# Revit family: РИДАН_Соленоидный клапан EV220WR(DN65_100)
name_source: partatom
category: Арматура трубопроводов
units: mm (PartAtom-declared; Revit-internal decimal feet)

## family parameters
Всегда вертикально = Да
На основе рабочей плоскости = Нет
Общий = Нет
При загрузке вырезать с полостями = Нет
Размер круглого соединителя = Использовать диаметр
Тип детали = Нормальный

## types (9) — shared parameters
ADSK_Версия Revit = 2019
ADSK_Версия семейства = 1.0
ADSK_Единица измерения = шт.
ADSK_Завод-изготовитель = ООО «Ридан-Трейд»
ADSK_Количество = 1
ADSK_Количество фаз = 1
ADSK_Коэффициент мощности = 1
ADSK_Потеря давления жидкости = 0.0 Па
ADSK_Расход жидкости = 0.0 л/с
LT = EV220WR _DN65_100
Table = EV220WR _DN65_100_1

## per-type parameters (varying)
- DN65+RW3220AC: ADSK_Диаметр условный=65 мм; ADSK_Код изделия=016D6065R; ADSK_Марка=EV220WR DN65; ADSK_Масса=15.1; ADSK_Наименование=Клапан электромагнитный EV220WR, G 2 1/2, Ду 65 мм, EPDM, нормально закрытый; ADSK_Напряжение=230 В; ADSK_Номинальная мощность=16 Вт; ADSK_Полная мощность=16 В·А; ADSK_Пропускная способность=12.2 л/с; a=2 мм; b=18 мм; c=10 мм; d=100 мм; e=199 мм; f=78 мм; g=98 мм; h=114 мм; i=118 мм; j=185 мм; k=40 мм; l=74 мм; m=92 мм; n=116 мм; o=178 мм; p=142 мм; r=114 мм; s=42 мм; t=137 мм; t1=158 мм; t2=79 мм; t3=83 мм; Катушка=Влж_Катушка EV220WR : RW3220AC; Катушка_1=RW3220AC; УГО_Длина=259 мм
- DN65+RW3024AC: ADSK_Диаметр условный=65 мм; ADSK_Код изделия=016D6065R; ADSK_Марка=EV220WR DN65; ADSK_Масса=15.1; ADSK_Наименование=Клапан электромагнитный EV220WR, G 2 1/2, Ду 65 мм, EPDM, нормально закрытый; ADSK_Напряжение=24 В; ADSK_Номинальная мощность=24 Вт; ADSK_Полная мощность=24 В·А; ADSK_Пропускная способность=12.2 л/с; a=2 мм; b=18 мм; c=10 мм; d=100 мм; e=199 мм; f=78 мм; g=98 мм; h=114 мм; i=118 мм; j=185 мм; k=40 мм; l=74 мм; m=92 мм; n=116 мм; o=178 мм; p=142 мм; r=114 мм; s=42 мм; t=137 мм; t1=158 мм; t2=79 мм; t3=83 мм; Катушка=Влж_Катушка EV220WR : RW3024AC; Катушка_1=RW3024AC; УГО_Длина=259 мм
- DN65+RW3024DC: ADSK_Диаметр условный=65 мм; ADSK_Код изделия=016D6065R; ADSK_Марка=EV220WR DN65; ADSK_Масса=15.1; ADSK_Наименование=Клапан электромагнитный EV220WR, G 2 1/2, Ду 65 мм, EPDM, нормально закрытый; ADSK_Напряжение=24 В; ADSK_Номинальная мощность=14 Вт; ADSK_Полная мощность=14 В·А; ADSK_Пропускная способность=12.2 л/с; a=2 мм; b=18 мм; c=10 мм; d=100 мм; e=199 мм; f=78 мм; g=98 мм; h=114 мм; i=118 мм; j=185 мм; k=40 мм; l=74 мм; m=92 мм; n=116 мм; o=178 мм; p=142 мм; r=114 мм; s=42 мм; t=137 мм; t1=158 мм; t2=79 мм; t3=83 мм; Катушка=Влж_Катушка EV220WR : RW3024DC; Катушка_1=RW3024DC; УГО_Длина=259 мм
- DN80+RW3220AC: ADSK_Диаметр условный=80 мм; ADSK_Код изделия=016D6080R; ADSK_Марка=EV220WR DN80; ADSK_Масса=17; ADSK_Наименование=Клапан электромагнитный EV220WR, G 3, Ду 80 мм, EPDM, нормально закрытый; ADSK_Напряжение=230 В; ADSK_Номинальная мощность=16 Вт; ADSK_Полная мощность=16 В·А; ADSK_Пропускная способность=19.4 л/с; a=3 мм; b=16 мм; c=38 мм; d=82 мм; e=163 мм; f=93 мм; g=125 мм; h=126 мм; i=132 мм; j=200 мм; k=50 мм; l=86 мм; m=102 мм; n=126 мм; o=195 мм; p=137 мм; r=103 мм; s=42 мм; t=151 мм; t1=174 мм; t2=87 мм; t3=94 мм; Катушка=Влж_Катушка EV220WR : RW3220AC; Катушка_1=RW3220AC; УГО_Длина=278 мм
- DN80+RW3024AC: ADSK_Диаметр условный=80 мм; ADSK_Код изделия=016D6080R; ADSK_Марка=EV220WR DN80; ADSK_Масса=17; ADSK_Наименование=Клапан электромагнитный EV220WR, G 3, Ду 80 мм, EPDM, нормально закрытый; ADSK_Напряжение=24 В; ADSK_Номинальная мощность=24 Вт; ADSK_Полная мощность=24 В·А; ADSK_Пропускная способность=19.4 л/с; a=3 мм; b=16 мм; c=38 мм; d=82 мм; e=163 мм; f=93 мм; g=125 мм; h=126 мм; i=132 мм; j=200 мм; k=50 мм; l=86 мм; m=102 мм; n=126 мм; o=195 мм; p=137 мм; r=103 мм; s=42 мм; t=151 мм; t1=174 мм; t2=87 мм; t3=94 мм; Катушка=Влж_Катушка EV220WR : RW3024AC; Катушка_1=RW3024AC; УГО_Длина=278 мм
- DN80+RW3024DC: ADSK_Диаметр условный=80 мм; ADSK_Код изделия=016D6080R; ADSK_Марка=EV220WR DN80; ADSK_Масса=17; ADSK_Наименование=Клапан электромагнитный EV220WR, G 3, Ду 80 мм, EPDM, нормально закрытый; ADSK_Напряжение=24 В; ADSK_Номинальная мощность=14 Вт; ADSK_Полная мощность=14 В·А; ADSK_Пропускная способность=19.4 л/с; a=3 мм; b=16 мм; c=38 мм; d=82 мм; e=163 мм; f=93 мм; g=125 мм; h=126 мм; i=132 мм; j=200 мм; k=50 мм; l=86 мм; m=102 мм; n=126 мм; o=195 мм; p=137 мм; r=103 мм; s=42 мм; t=151 мм; t1=174 мм; t2=87 мм; t3=94 мм; Катушка=Влж_Катушка EV220WR : RW3024DC; Катушка_1=RW3024DC; УГО_Длина=278 мм
- DN100+RW3220AC: ADSK_Диаметр условный=100 мм; ADSK_Код изделия=016D6100R; ADSK_Марка=EV220WR DN100; ADSK_Масса=23.2; ADSK_Наименование=Клапан электромагнитный EV220WR, G 4, Ду 100 мм, EPDM, нормально закрытый; ADSK_Напряжение=230 В; ADSK_Номинальная мощность=16 Вт; ADSK_Полная мощность=16 В·А; ADSK_Пропускная способность=30.3 л/с; a=3 мм; b=18 мм; c=46 мм; d=108 мм; e=216 мм; f=114 мм; g=150 мм; h=150 мм; i=156 мм; j=220 мм; k=57 мм; l=94 мм; m=115 мм; n=143 мм; o=220 мм; p=166 мм; r=128 мм; s=50 мм; t=170 мм; t1=196 мм; t2=98 мм; t3=104 мм; Катушка=Влж_Катушка EV220WR : RW3220AC; Катушка_1=RW3220AC; УГО_Длина=350 мм
- DN100+RW3024AC: ADSK_Диаметр условный=100 мм; ADSK_Код изделия=016D6100R; ADSK_Марка=EV220WR DN100; ADSK_Масса=23.2; ADSK_Наименование=Клапан электромагнитный EV220WR, G 4, Ду 100 мм, EPDM, нормально закрытый; ADSK_Напряжение=24 В; ADSK_Номинальная мощность=24 Вт; ADSK_Полная мощность=24 В·А; ADSK_Пропускная способность=30.3 л/с; a=3 мм; b=18 мм; c=46 мм; d=108 мм; e=216 мм; f=114 мм; g=150 мм; h=150 мм; i=156 мм; j=220 мм; k=57 мм; l=94 мм; m=115 мм; n=143 мм; o=220 мм; p=166 мм; r=128 мм; s=50 мм; t=170 мм; t1=196 мм; t2=98 мм; t3=104 мм; Катушка=Влж_Катушка EV220WR : RW3024AC; Катушка_1=RW3024AC; УГО_Длина=350 мм
- DN100+RW3024DC: ADSK_Диаметр условный=100 мм; ADSK_Код изделия=016D6100R; ADSK_Марка=EV220WR DN100; ADSK_Масса=23.2; ADSK_Наименование=Клапан электромагнитный EV220WR, G 4, Ду 100 мм, EPDM, нормально закрытый; ADSK_Напряжение=24 В; ADSK_Номинальная мощность=14 Вт; ADSK_Полная мощность=14 В·А; ADSK_Пропускная способность=30.3 л/с; a=3 мм; b=18 мм; c=46 мм; d=108 мм; e=216 мм; f=114 мм; g=150 мм; h=150 мм; i=156 мм; j=220 мм; k=57 мм; l=94 мм; m=115 мм; n=143 мм; o=220 мм; p=166 мм; r=128 мм; s=50 мм; t=170 мм; t1=196 мм; t2=98 мм; t3=104 мм; Катушка=Влж_Катушка EV220WR : RW3024DC; Катушка_1=RW3024DC; УГО_Длина=350 мм
